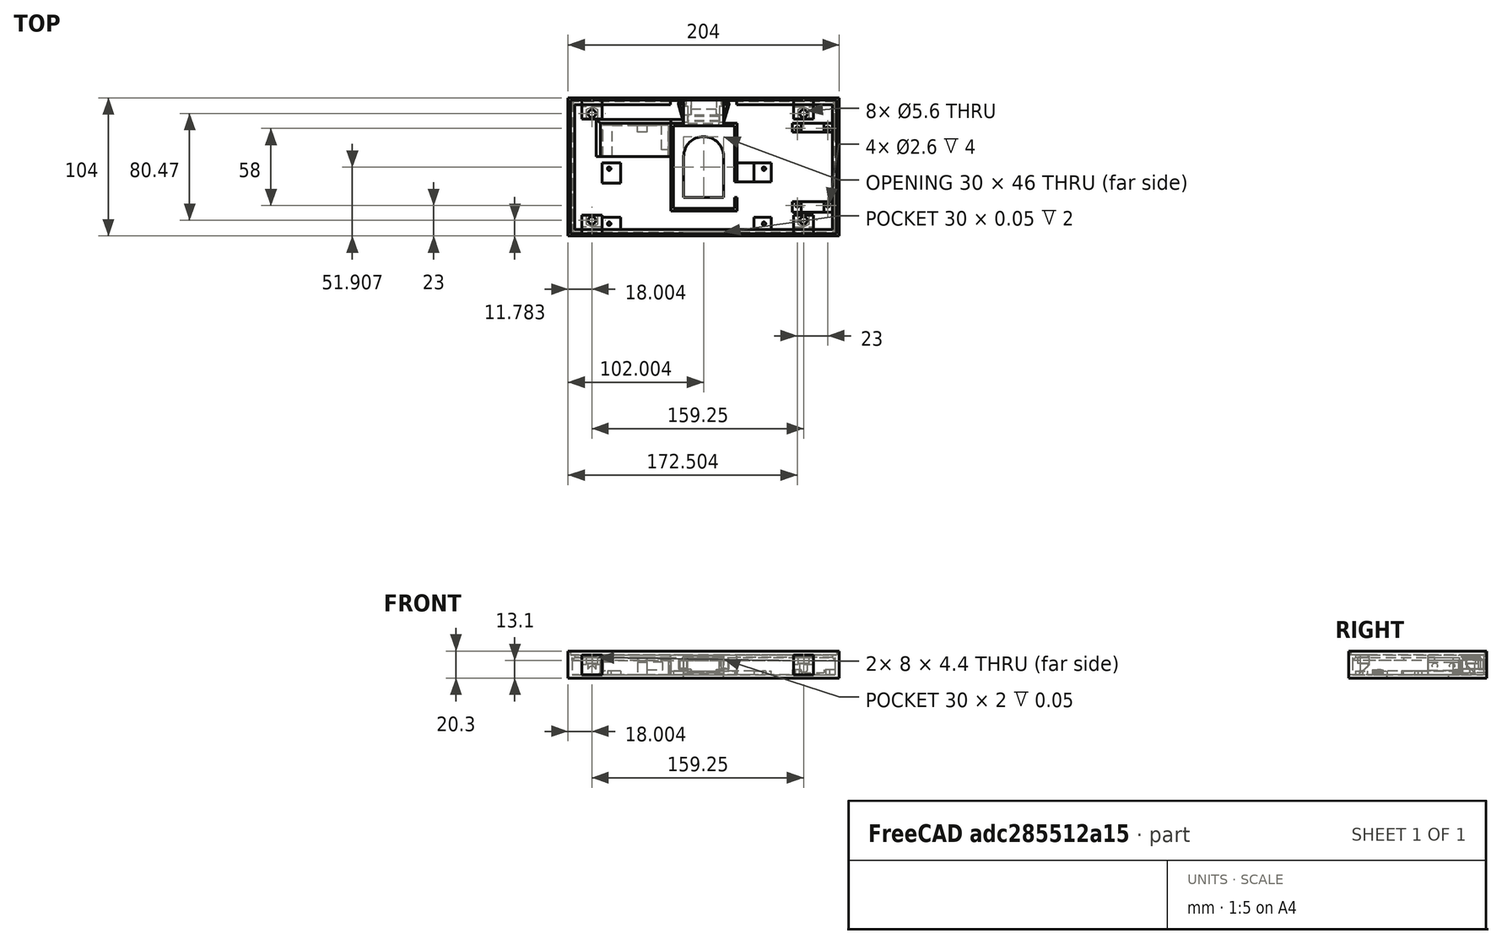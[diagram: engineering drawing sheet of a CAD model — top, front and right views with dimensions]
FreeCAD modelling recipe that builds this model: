
FCSTD DOCUMENT  (FreeCAD 0.18.4R)
Label: lamp.base
License: All rights reserved
LicenseURL: http://en.wikipedia.org/wiki/All_rights_reserved
objects: Part::Feature×5, Part::Part2DObjectPython×5, Part::Extrusion×2, Part::Cut×2, Part::MultiFuse×1
note: 15 computed .brp shape members not serialized (recipe doc carries the construction recipe); baked Part::Feature solids carry a one-line shape summary decoded from their .brp

FEATURE [Part::Feature] Fusion_rev_child0_child0_solid  label="Fusion (Rev).0.0 (Solid)"
  shape: bbox 15 x 15.78 x 15 mm, 15 faces (baked)
FEATURE [Part::Feature] Fusion_rev_child1_child0_solid  label="Fusion (Rev).1.0 (Solid)"
  shape: bbox 15 x 15.75 x 15 mm, 15 faces (baked)
FEATURE [Part::Feature] Fusion_rev_child3_child0_solid  label="Fusion (Rev).3.0 (Solid)"
  shape: bbox 15 x 15.75 x 15 mm, 15 faces (baked)
FEATURE [Part::Feature] Fusion_rev_child2_child0_solid  label="Fusion (Rev).2.0 (Solid)"
  shape: bbox 15 x 15.78 x 15 mm, 15 faces (baked)
FEATURE [Part::MultiFuse] Fusion076089004005008002002002002003004002007
FEATURE [Part::Part2DObjectPython] Line  # Draft 2D object (typed FeaturePython)
  ChamferSize = 0
  Closed = false
  End = (107.384,-626.213,9.00025)
  FilletRadius = 0
  Length = 60.3801
  MakeFace = true
  Placement = pos=(47.0036,-626.213,9.00025) rot=(0,0,1;0rad)
  Points = (2) [(0,0,0),(60.3801,0,0)]
  Start = (47.0036,-626.213,9.00025)
  Subdivisions = 0
FEATURE [Part::Part2DObjectPython] Line001  # Draft 2D object (typed FeaturePython)
  ChamferSize = 0
  Closed = false
  End = (96.0036,-520.181,9.00025)
  FilletRadius = 0
  Length = 147.032
  MakeFace = true
  Placement = pos=(96.0036,-667.213,9.00025) rot=(0,0,1;0rad)
  Points = (2) [(0,0,0),(0,147.032,0)]
  Start = (96.0036,-667.213,9.00025)
  Subdivisions = 0
FEATURE [Part::Part2DObjectPython] Line002  # Draft 2D object (typed FeaturePython)
  ChamferSize = 0
  Closed = false
  End = (96.0036,-626.213,-73.5805)
  FilletRadius = 0
  Length = 97.5805
  MakeFace = true
  Placement = pos=(96.0036,-626.213,24) rot=(1,0,0;1.5708rad)
  Points = (2) [(0,0,0),(0,-97.5805,-4.54747e-13)]
  Start = (96.0036,-626.213,24)
  Subdivisions = 0
  Support = -> [Fusion076089004005008002002002002003004002007]
FEATURE [Part::Part2DObjectPython] Line003  # Draft 2D object (typed FeaturePython)
  ChamferSize = 0
  Closed = false
  End = (23.4114,-702.63,9)
  FilletRadius = 0
  Length = 105.4
  MakeFace = true
  Placement = pos=(96.0036,-626.213,9.00025) rot=(0,0,1;0rad)
  Points = (2) [(0,0,0),(-72.5922,-76.4173,-0.00025217)]
  Start = (96.0036,-626.213,9.00025)
  Subdivisions = 0
  Support = -> [Fusion076089004005008002002002002003004002007]
FEATURE [Part::Part2DObjectPython] Rectangle  # Draft 2D object (typed FeaturePython)
  ChamferSize = 0
  Columns = 1
  FilletRadius = 0
  Height = 28
  Length = 49
  MakeFace = true
  Placement = pos=(47.0036,-626.213,9.00025) rot=(0,0,1;0rad)
  Rows = 1
FEATURE [Part::Extrusion] Extrusion
  Base = -> Rectangle
  Dir = (0,0,14.9997)
  DirMode = 0
  FaceMakerClass = Part::FaceMakerBullseye
  LengthFwd = 0
  LengthRev = 0
  Solid = true
  Symmetric = false
FEATURE [Part::Cut] Cut
  Base = -> Fusion076089004005008002002002002003004002007
  Tool = -> Extrusion
FEATURE [Part::Cut] Cut279012004
  Tool = -> Extrusion
FEATURE [Part::Feature] Face
  Placement = pos=(255.302,-5.37176,8.7e-14) rot=(0,0,1;0rad)
  shape: bbox 7.839e-07 x 14.1 x 3 mm, 1 faces, 0 solids (baked)
FEATURE [Part::Extrusion] Extrusion001
  Base = -> Face
  Dir = (-12.55,0,-9e-15)
  DirMode = 0
  FaceMakerClass = Part::FaceMakerBullseye
  LengthFwd = 0
  LengthRev = 0
  Solid = true
  Symmetric = false
